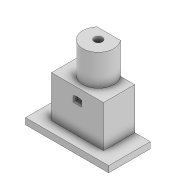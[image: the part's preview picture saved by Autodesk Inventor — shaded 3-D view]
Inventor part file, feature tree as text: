
AUTODESK INVENTOR PART (.ipt)
format: ipt  version: 2022 (Build 260153000, 153)  size: 177,664 bytes
history: native  units: mm
features: extrude x9, sketch x9, projected_geometry x2
ambient origin geometry x8: Origin, YZ Plane, XZ Plane, XY Plane, X Axis, Y Axis, Z Axis, Center Point
bodies: Solid1 (feature_tree)
feature tree (20):
  extrude  "Extrusion1"  Depth=25.0mm
  extrude  "Extrusion2"  Depth=20.0mm TaperAngle=0.0deg
  extrude  "Extrusion3"  Depth=100.0mm TaperAngle=0.0deg
  extrude  "Extrusion4"  Depth=15.0mm TaperAngle=0.0deg
  extrude  "Extrusion6"  Depth=40.0mm
  extrude  "Extrusion8"  Depth=10.0mm TaperAngle=0.0deg
  extrude  "Extrusion9"  Depth=2.0mm
  extrude  "Extrusion10"  Depth=3.0mm
  extrude  "Extrusion11"  Depth=15.0mm
  sketch  "Sketch1"  dims[d0=12.2mm d1=25.0mm]
  sketch  "Sketch2"  dims[d2=20.0mm d3=20.0mm d4=0.0mm]
  sketch  "Sketch3"  dims[d5=3.9mm d6=100.0mm d7=0.0mm]
  projected_geometry  "Projected Loop1"
  sketch  "Sketch4"  dims[d8=15.0mm d9=15.0mm d10=0.0mm]
  sketch  "Sketch6"  dims[d11=30.0mm d12=40.0mm]
  sketch  "Sketch8"  dims[d13=3.0mm d14=0.0mm d21=10.0mm d22=0.0mm]
  sketch  "Sketch9"  dims[d26=100.0mm d27=0.0mm d28=2.0mm]
  projected_geometry  "Projected Loop3"
  sketch  "Sketch10"  dims[d29=2.0mm d30=3.0mm]
  sketch  "Sketch11"  dims[d31=2.0mm d32=0.0mm d33=9.8mm d34=15.0mm d35=0.0mm d36=100.0mm d37=0.0mm]
